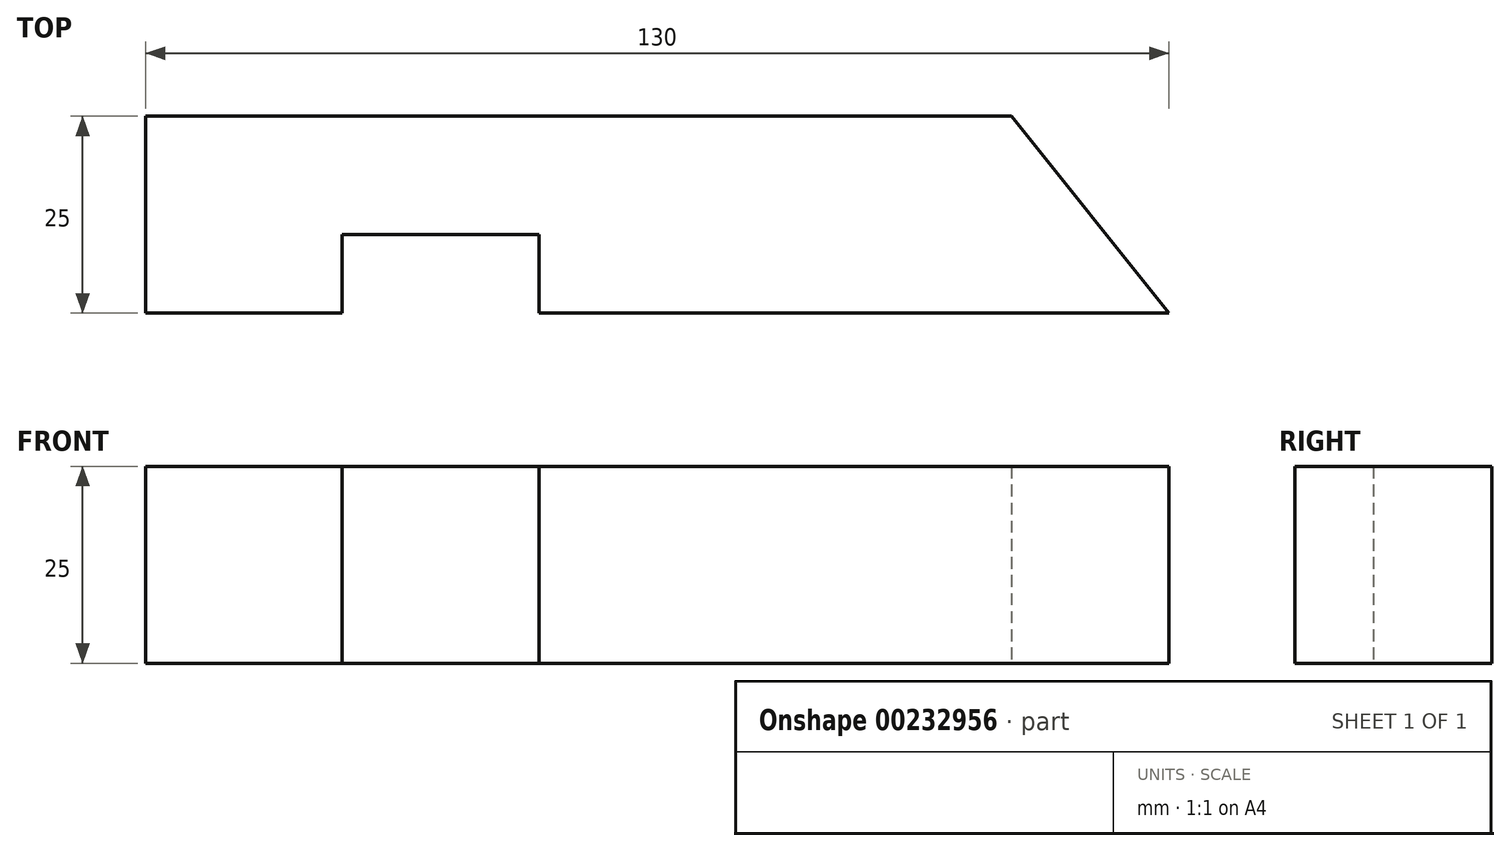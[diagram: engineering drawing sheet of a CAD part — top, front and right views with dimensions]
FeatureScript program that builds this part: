
annotation { "Feature Type Name" : "Feature", "Feature Type Description" : "" }
export const myFeature = defineFeature(function(context is Context, id is Id, definition is map)
    precondition{}
    {
        {
            var Q0;
            Q0=qCreatedBy(makeId("Top.planeOp"),FACE);
            var sketch = newSketch(context, id + "F0", { "sketchPlane" : qUnion([Q0])});
            skLineSegment(sketch, "E0", {"start": v(-59.07, -17.75) * mm, "end": v(-34.07, -17.75) * mm});
            skLineSegment(sketch, "E1", {"start": v(-34.07, -17.75) * mm, "end": v(-34.07, -7.75) * mm});
            skLineSegment(sketch, "E2", {"start": v(-34.07, -7.75) * mm, "end": v(-9.07, -7.75) * mm});
            skLineSegment(sketch, "E3", {"start": v(-9.07, -7.75) * mm, "end": v(-9.07, -17.75) * mm});
            skLineSegment(sketch, "E4", {"start": v(-9.07, -17.75) * mm, "end": v(70.93, -17.75) * mm});
            skLineSegment(sketch, "E5", {"start": v(-59.07, -17.75) * mm, "end": v(-59.07, 7.25) * mm});
            skLineSegment(sketch, "E6", {"start": v(-59.07, 7.25) * mm, "end": v(50.93, 7.25) * mm});
            skLineSegment(sketch, "E7", {"start": v(50.93, 7.25) * mm, "end": v(70.93, -17.75) * mm});
            skSolve(sketch);
        }
        {
            var Q0;
            Q0=makeQuery(id+"F0.imprint","IMPRINT",FACE,{"disambiguationData":[TD([[makeQuery(id+"F0.imprint","IMPRINT",EDGE,{"derivedFrom":sQuery(id+"F0.wireOp",EDGE,"E0")}),1.0]])]});
            extrude(context, id + "F1", {"entities" : qUnion([Q0]), "depth" : 25 * mm});
        }
    });
